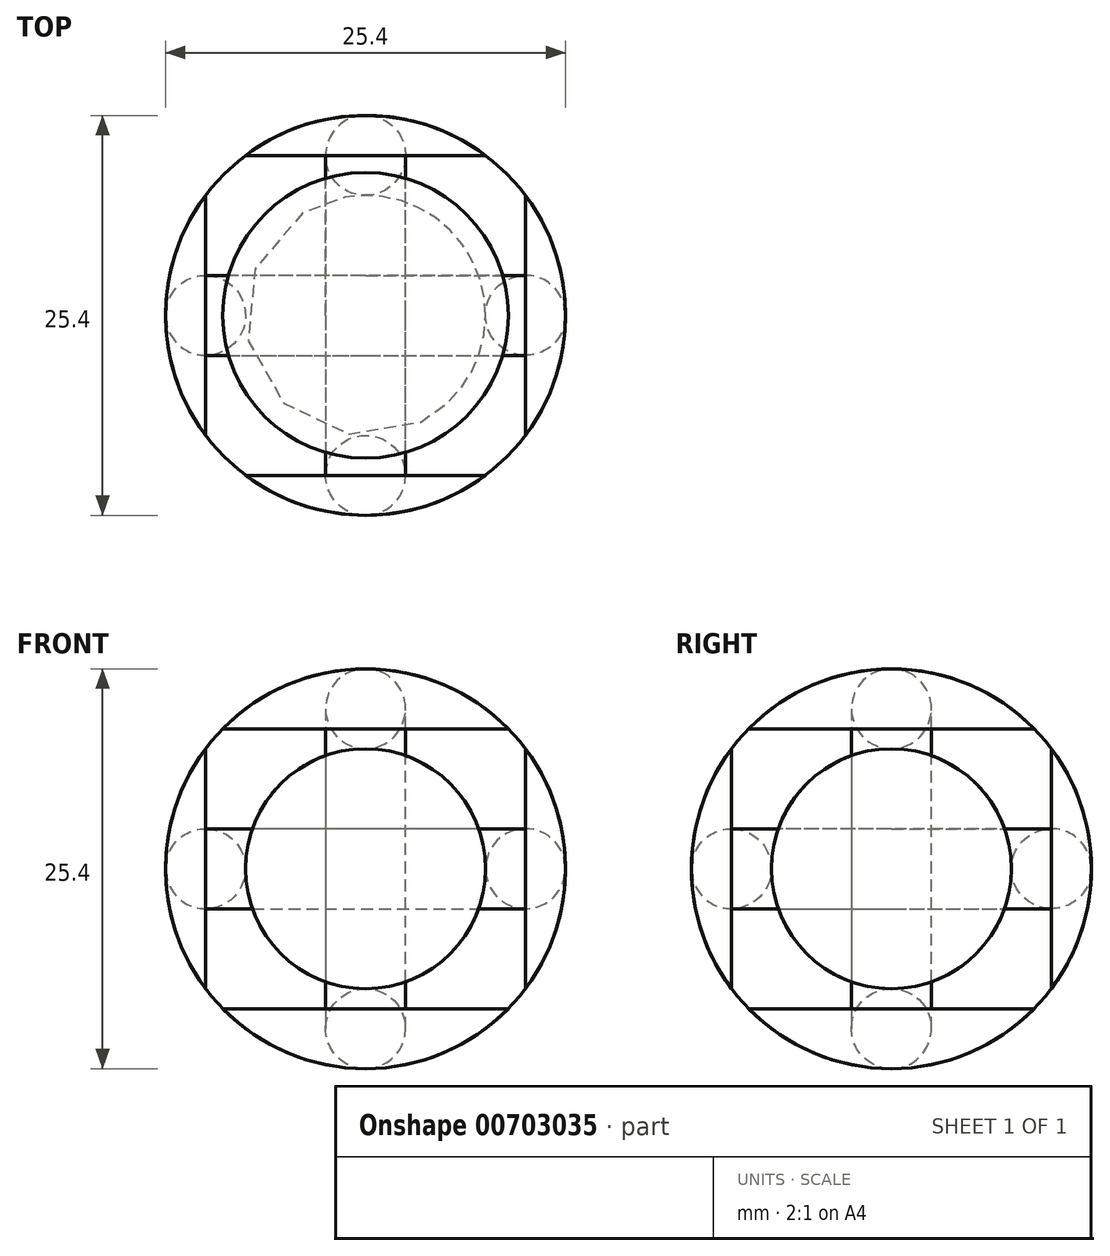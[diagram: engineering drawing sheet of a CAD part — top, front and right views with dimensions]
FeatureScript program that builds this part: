
annotation { "Feature Type Name" : "Feature", "Feature Type Description" : "" }
export const myFeature = defineFeature(function(context is Context, id is Id, definition is map)
    precondition{}
    {
        {
            var Q0;
            Q0=qCreatedBy(makeId("Top.planeOp"),FACE);
            var sketch = newSketch(context, id + "F0", { "sketchPlane" : qUnion([Q0])});
            skCircle(sketch, "E0", {"center": v(0, 0) * mm, "radius": 12.7 * mm});
            skLineSegment(sketch, "E1", {"start": v(0, 12.7) * mm, "end": v(0, -12.7) * mm});
            skSolve(sketch);
        }
        {
            var Q0;
            {var subQ0=sQuery(id+"F0.wireOp",EDGE,"E1");Q0=makeQuery(id+"F0.imprint","IMPRINT",FACE,{"disambiguationData":[TD([[makeQuery(id+"F0.imprint","IMPRINT",EDGE,{"derivedFrom":subQ0}),-1.0]])]});}
            var Q1;
            Q1=sQuery(id+"F0.wireOp",EDGE,"E1");
            revolve(context, id + "F1", {"surfaceOperationType" : NewSurfaceOperationType.NEW, "entities" : qUnion([Q0]), "axis" : qUnion([Q1]), "revolveType" : RevolveType.FULL});
        }
        {
            var Q0;
            Q0=qCreatedBy(makeId("Top.planeOp"),FACE);
            var sketch = newSketch(context, id + "F2", { "sketchPlane" : qUnion([Q0])});
            skLineSegment(sketch, "E2.bottom", {"start": v(10.16, 10.16) * mm, "end": v(-10.16, 10.16) * mm});
            skLineSegment(sketch, "E2.top", {"start": v(10.16, -10.16) * mm, "end": v(-10.16, -10.16) * mm});
            skLineSegment(sketch, "E2.left", {"start": v(10.16, 10.16) * mm, "end": v(10.16, -10.16) * mm});
            skLineSegment(sketch, "E2.right", {"start": v(-10.16, 10.16) * mm, "end": v(-10.16, -10.16) * mm});
            skPoint(sketch, "E2.middle", {"position": v(0, 0) * mm});
            skSolve(sketch);
        }
        {
            var Q0;
            Q0=makeQuery(id+"F2.imprint","IMPRINT",FACE,{"disambiguationData":[TD([[makeQuery(id+"F2.imprint","IMPRINT",EDGE,{"derivedFrom":sQuery(id+"F2.wireOp",EDGE,"E2.bottom")}),1.0]])]});
            extrude(context, id + "F3", {"entities" : qUnion([Q0]), "operationType" : NewBodyOperationType.REMOVE, "endBound" : BoundingType.SYMMETRIC, "depth" : 17.78 * mm, "offsetDistance" : 25.4 * mm});
        }
        {
            var Q0;
            Q0=qCreatedBy(makeId("Top.planeOp"),FACE);
            var sketch = newSketch(context, id + "F4", { "sketchPlane" : qUnion([Q0])});
            skCircle(sketch, "E3", {"center": v(10.16, 0) * mm, "radius": 2.54 * mm});
            skLineSegment(sketch, "E4", {"start": v(0, 0) * mm, "end": v(0, -10.7) * mm});
            skSolve(sketch);
        }
        {
            var Q0;
            Q0=makeQuery(id+"F4.imprint","IMPRINT",FACE,{"disambiguationData":[TD([[makeQuery(id+"F4.imprint","IMPRINT",EDGE,{"derivedFrom":sQuery(id+"F4.wireOp",EDGE,"E3")}),1.0]])]});
            var Q1;
            Q1=sQuery(id+"F4.wireOp",EDGE,"E4");
            revolve(context, id + "F5", {"surfaceOperationType" : NewSurfaceOperationType.NEW, "entities" : qUnion([Q0]), "axis" : qUnion([Q1]), "revolveType" : RevolveType.FULL});
        }
        {
            var Q0;
            Q0=qCreatedBy(makeId("Top.planeOp"),FACE);
            var sketch = newSketch(context, id + "F6", { "sketchPlane" : qUnion([Q0])});
            skCircle(sketch, "E5", {"center": v(0, 10.16) * mm, "radius": 2.54 * mm});
            skLineSegment(sketch, "E6", {"start": v(0, 0) * mm, "end": v(14.6, 0) * mm});
            skSolve(sketch);
        }
        {
            var Q0;
            Q0 = qSketchRegion(id + "F6", true);
            var Q1;
            Q1=sQuery(id+"F6.wireOp",EDGE,"E6");
            revolve(context, id + "F7", {"surfaceOperationType" : NewSurfaceOperationType.NEW, "entities" : qUnion([Q0]), "axis" : qUnion([Q1]), "revolveType" : RevolveType.FULL});
        }
        {
            var Q0;
            Q0=qCreatedBy(makeId("Right.planeOp"),FACE);
            var sketch = newSketch(context, id + "F8", { "sketchPlane" : qUnion([Q0])});
            skCircle(sketch, "E7", {"center": v(10.16, 0) * mm, "radius": 2.54 * mm});
            skLineSegment(sketch, "E8", {"start": v(0, 0) * mm, "end": v(0, -14.5) * mm});
            skSolve(sketch);
        }
        {
            var Q0;
            Q0 = qSketchRegion(id + "F8", true);
            var Q1;
            Q1=sQuery(id+"F8.wireOp",EDGE,"E8");
            revolve(context, id + "F9", {"surfaceOperationType" : NewSurfaceOperationType.NEW, "entities" : qUnion([Q0]), "axis" : qUnion([Q1]), "revolveType" : RevolveType.FULL});
        }
    });
